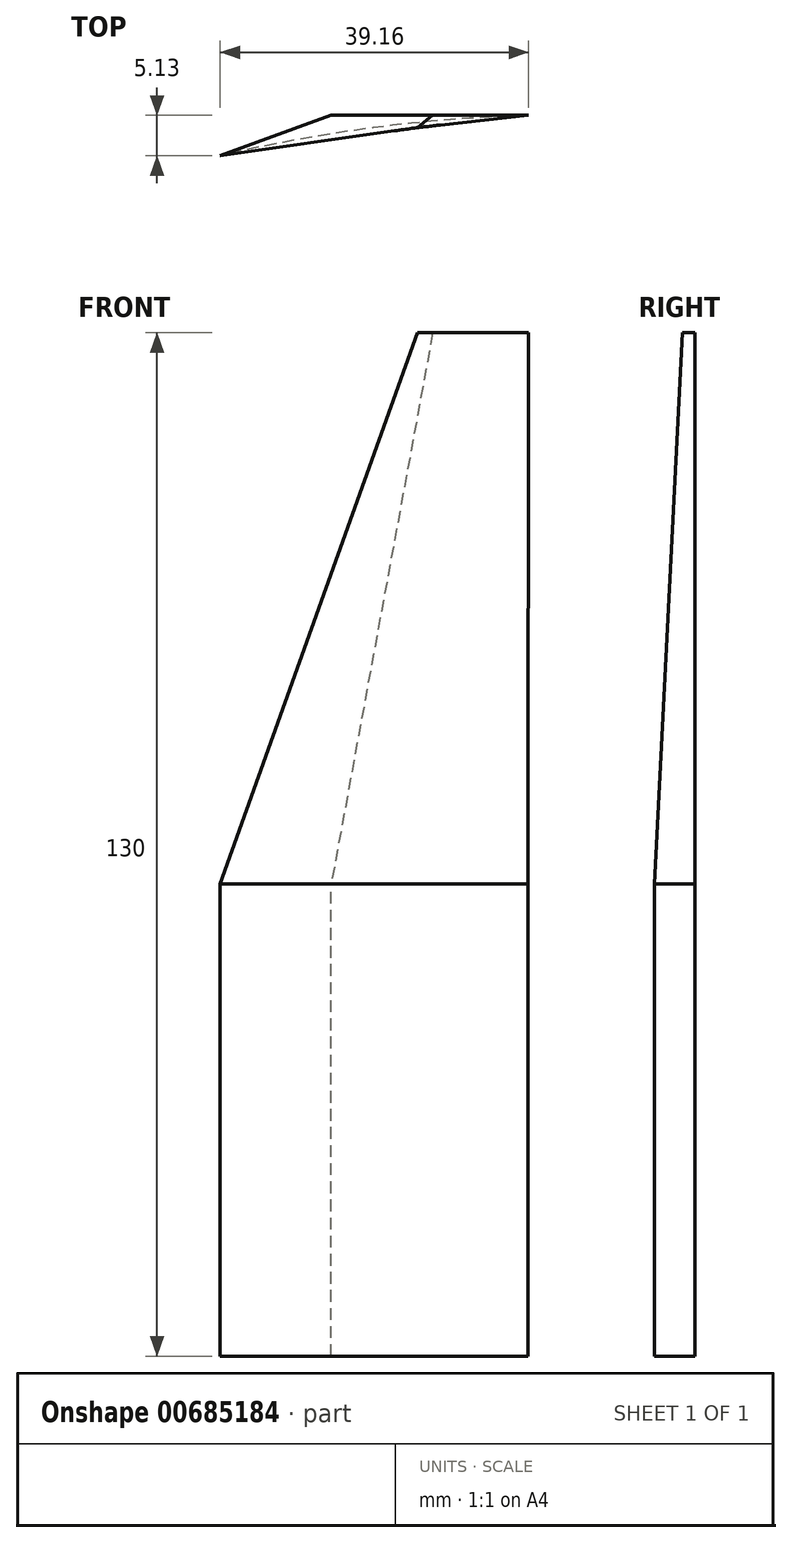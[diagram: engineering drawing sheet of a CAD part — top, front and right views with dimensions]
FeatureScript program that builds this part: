
annotation { "Feature Type Name" : "Feature", "Feature Type Description" : "" }
export const myFeature = defineFeature(function(context is Context, id is Id, definition is map)
    precondition{}
    {
        {
            var Q0;
            Q0=qCreatedBy(makeId("Top.planeOp"),FACE);
            var sketch = newSketch(context, id + "F0", { "sketchPlane" : qUnion([Q0])});
            skLineSegment(sketch, "E0", {"start": v(0, 0) * mm, "end": v(-14.1, -5.13) * mm});
            skLineSegment(sketch, "E1", {"start": v(0, 0) * mm, "end": v(25, 0) * mm});
            skArc(sketch, "E2", {"start": v(25, 0) * mm, "mid": v(5.32, -1.58) * mm, "end": v(-14.1, -5.13) * mm});
            skSolve(sketch);
        }
        {
            var Q0;
            Q0=makeQuery(id+"F0.imprint","IMPRINT",FACE,{"disambiguationData":[TD([[makeQuery(id+"F0.imprint","IMPRINT",EDGE,{"derivedFrom":sQuery(id+"F0.wireOp",EDGE,"E0")}),1.0]])]});
            cPlane(context, id + "F1", {"entities" : qUnion([Q0]), "cplaneType" : CPlaneType.OFFSET, "offset" : 60 * mm, "width" : 150 * mm, "height" : 150 * mm});
        }
        {
            var Q0;
            Q0=qCreatedBy(id+"F1.planeOp",FACE);
            var sketch = newSketch(context, id + "F2", { "sketchPlane" : qUnion([Q0])});
            skLineSegment(sketch, "E3.0", {"start": v(0, 0) * mm, "end": v(25, 0) * mm});
            skLineSegment(sketch, "E3.1", {"start": v(0, 0) * mm, "end": v(-14.1, -5.13) * mm});
            skArc(sketch, "E3.2", {"start": v(25, 0) * mm, "mid": v(5.32, -1.58) * mm, "end": v(-14.1, -5.13) * mm});
            skSolve(sketch);
        }
        {
            var Q0;
            Q0=qCreatedBy(id+"F1.planeOp",FACE);
            cPlane(context, id + "F3", {"entities" : qUnion([Q0]), "cplaneType" : CPlaneType.OFFSET, "offset" : 70 * mm, "width" : 150 * mm, "height" : 150 * mm});
        }
        {
            var Q0;
            Q0=qCreatedBy(id+"F3.planeOp",FACE);
            var sketch = newSketch(context, id + "F4", { "sketchPlane" : qUnion([Q0])});
            skLineSegment(sketch, "E4", {"start": v(12.9, 0) * mm, "end": v(10.97, -1.55) * mm});
            skLineSegment(sketch, "E5", {"start": v(10.97, -1.55) * mm, "end": v(25.06, 0) * mm});
            skLineSegment(sketch, "E6", {"start": v(25.06, 0) * mm, "end": v(12.9, 0) * mm});
            skSolve(sketch);
        }
        {
            var Q0;
            Q0=makeQuery(id+"F0.imprint","IMPRINT",FACE,{"disambiguationData":[TD([[makeQuery(id+"F0.imprint","IMPRINT",EDGE,{"derivedFrom":sQuery(id+"F0.wireOp",EDGE,"E0")}),1.0]])]});
            var Q1;
            Q1=makeQuery(id+"F2.imprint","IMPRINT",FACE,{"disambiguationData":[TD([[makeQuery(id+"F2.imprint","IMPRINT",EDGE,{"derivedFrom":sQuery(id+"F2.wireOp",EDGE,"E3.0")}),-1.0]])]});
            loft(context, id + "F5", {"sheetProfilesArray" : [{ "sheetProfileEntities" : qUnion([Q0]) }, { "sheetProfileEntities" : qUnion([Q1]) }]});
        }
        {
            var Q1;
            Q1=makeQuery(id+"F4.imprint","IMPRINT",FACE,{"disambiguationData":[TD([[makeQuery(id+"F4.imprint","IMPRINT",EDGE,{"derivedFrom":sQuery(id+"F4.wireOp",EDGE,"E4")}),1.0]])]});
            var Q2;
            Q2=makeQuery(id+"F5.opLoft","CAP_FACE",FACE,{"disambiguationData":[OSD([makeQuery(id+"F2.imprint","IMPRINT",FACE,{"disambiguationData":[TD([[makeQuery(id+"F2.imprint","IMPRINT",EDGE,{"derivedFrom":sQuery(id+"F2.wireOp",EDGE,"E3.0")}),-1.0]])]})])],"isStart":true});
            loft(context, id + "F6", {"operationType" : NewBodyOperationType.ADD, "sheetProfilesArray" : [{ "sheetProfileEntities" : qUnion([Q1]) }, { "sheetProfileEntities" : qUnion([Q2]) }]});
        }
    });
